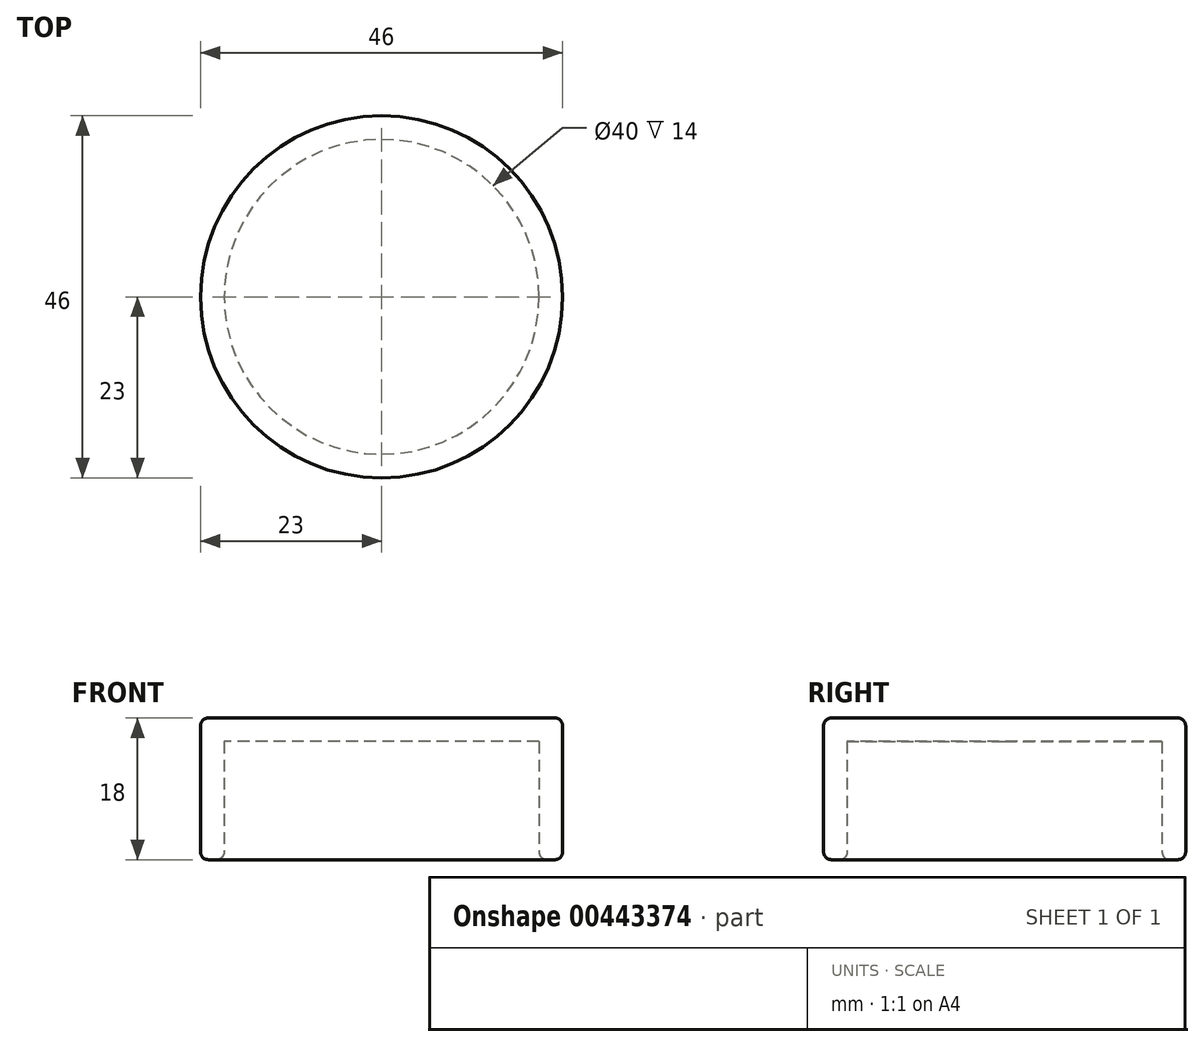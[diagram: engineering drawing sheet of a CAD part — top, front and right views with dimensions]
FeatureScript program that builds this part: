
annotation { "Feature Type Name" : "Feature", "Feature Type Description" : "" }
export const myFeature = defineFeature(function(context is Context, id is Id, definition is map)
    precondition{}
    {
        {
            var Q0;
            Q0=qCreatedBy(makeId("Top.planeOp"),FACE);
            var sketch = newSketch(context, id + "F0", { "sketchPlane" : qUnion([Q0])});
            skCircle(sketch, "E0", {"center": v(0, 0) * mm, "radius": 23 * mm});
            skCircle(sketch, "E1", {"center": v(0, 0) * mm, "radius": 20 * mm});
            skSolve(sketch);
        }
        {
            var Q0;
            Q0=makeQuery(id+"F0.imprint","IMPRINT",FACE,{"disambiguationData":[TD([[makeQuery(id+"F0.imprint","IMPRINT",EDGE,{"derivedFrom":sQuery(id+"F0.wireOp",EDGE,"E0")}),1.0]])]});
            extrude(context, id + "F1", {"entities" : qUnion([Q0]), "depth" : 15 * mm});
        }
        {
            var Q0;
            Q0=makeQuery(id+"F1.opExtrude","CAP_FACE",FACE,{"disambiguationData":[OSD([sQuery(id+"F0.wireOp",EDGE,"E0"),sQuery(id+"F0.wireOp",EDGE,"E1")])],"isStart":false});
            var sketch = newSketch(context, id + "F2", { "sketchPlane" : qUnion([Q0])});
            skCircle(sketch, "E2", {"center": v(0, 0) * mm, "radius": 23 * mm});
            skSolve(sketch);
        }
        {
            var Q0;
            Q0 = qSketchRegion(id + "F2", true);
            extrude(context, id + "F3", {"entities" : qUnion([Q0]), "operationType" : NewBodyOperationType.ADD, "depth" : 3 * mm});
        }
        {
            var Q0;
            Q0=makeQuery(id+"F1.opExtrude","CAP_EDGE",EDGE,{"disambiguationData":[OSD([sQuery(id+"F0.wireOp",EDGE,"E0")])],"isStart":true});
            var Q1;
            Q1=makeQuery(id+"F3.opExtrude","CAP_EDGE",EDGE,{"disambiguationData":[OSD([sQuery(id+"F2.wireOp",EDGE,"E2")])],"isStart":false});
            fillet(context, id + "F4", {"entities" : qUnion([Q0, Q1]), "radius" : 1 * mm, "tangentPropagation" : true, "allowEdgeOverflow" : false});
        }
        {
            var Q0;
            Q0=makeQuery(id+"F1.opExtrude","CAP_EDGE",EDGE,{"disambiguationData":[OSD([sQuery(id+"F0.wireOp",EDGE,"E1")])],"isStart":true});
            fillet(context, id + "F5", {"entities" : qUnion([Q0]), "radius" : 1 * mm, "tangentPropagation" : true, "allowEdgeOverflow" : false});
        }
    });
